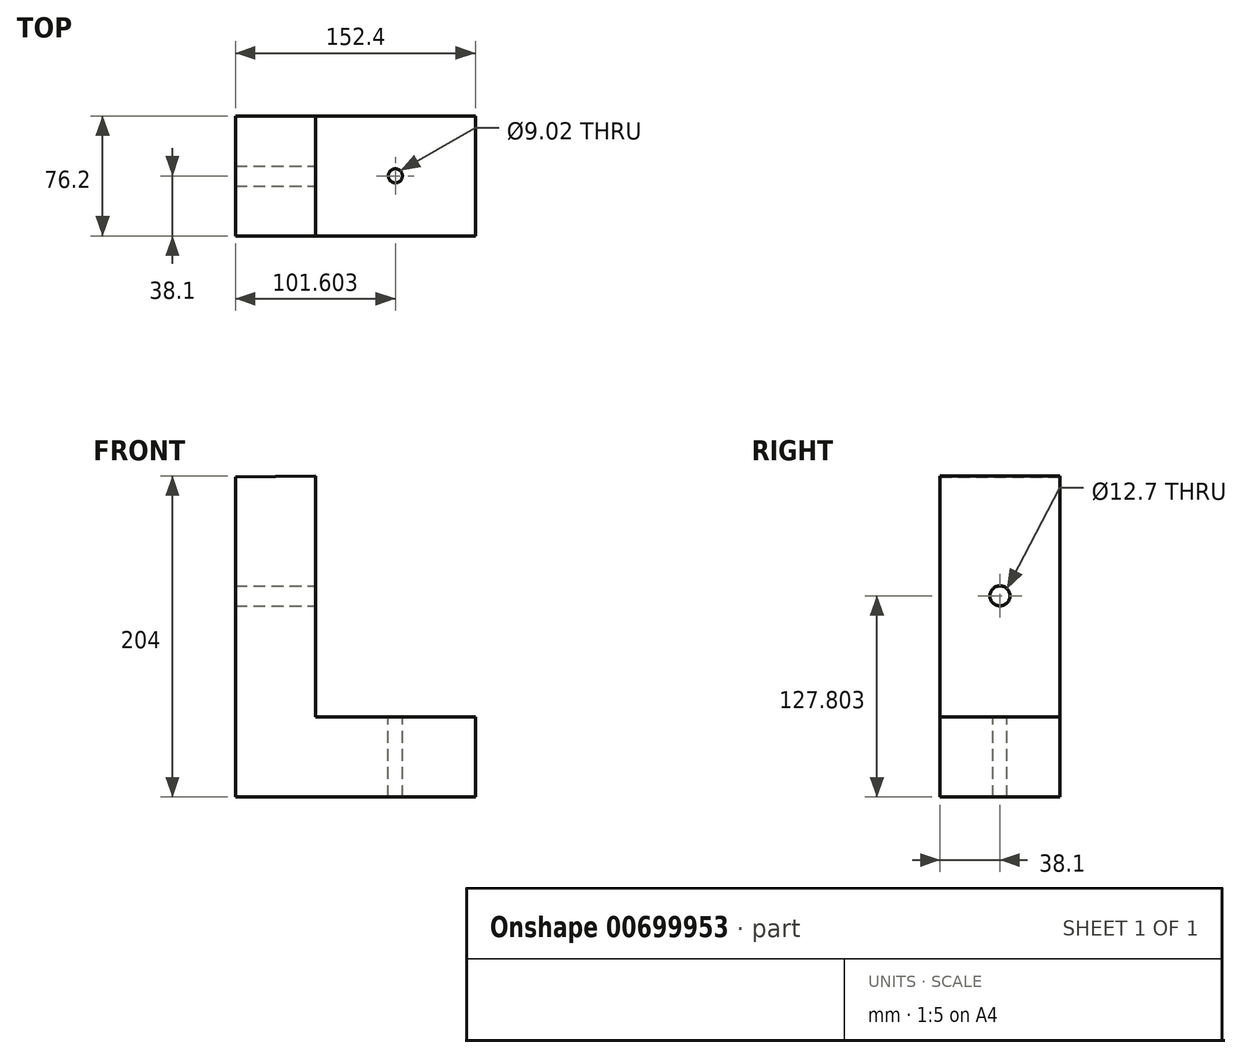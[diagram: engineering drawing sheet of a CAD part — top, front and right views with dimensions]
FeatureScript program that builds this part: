
annotation { "Feature Type Name" : "Feature", "Feature Type Description" : "" }
export const myFeature = defineFeature(function(context is Context, id is Id, definition is map)
    precondition{}
    {
        {
            var Q0;
            Q0=qCreatedBy(makeId("Front.planeOp"),FACE);
            var sketch = newSketch(context, id + "F0", { "sketchPlane" : qUnion([Q0])});
            skLineSegment(sketch, "E0", {"start": v(-81.87, 120.06) * mm, "end": v(-81.87, -83.14) * mm});
            skLineSegment(sketch, "E1", {"start": v(-81.87, -83.14) * mm, "end": v(70.53, -83.14) * mm});
            skLineSegment(sketch, "E2", {"start": v(70.53, -83.14) * mm, "end": v(70.53, -32.34) * mm});
            skLineSegment(sketch, "E3", {"start": v(70.53, -32.34) * mm, "end": v(-31.07, -32.34) * mm});
            skLineSegment(sketch, "E4", {"start": v(-31.07, -32.34) * mm, "end": v(-31.07, 120.86) * mm});
            skLineSegment(sketch, "E5", {"start": v(-31.07, 120.86) * mm, "end": v(-81.87, 120.06) * mm});
            skSolve(sketch);
        }
        {
            var Q0;
            Q0=makeQuery(id+"F0.imprint","IMPRINT",FACE,{"disambiguationData":[TD([[makeQuery(id+"F0.imprint","IMPRINT",EDGE,{"derivedFrom":sQuery(id+"F0.wireOp",EDGE,"E0")}),1.0]])]});
            extrude(context, id + "F1", {"entities" : qUnion([Q0]), "depth" : 76.2 * mm, "offsetDistance" : 25.4 * mm});
        }
        {
            var Q0;
            Q0=qCreatedBy(makeId("Right.planeOp"),FACE);
            var sketch = newSketch(context, id + "F2", { "sketchPlane" : qUnion([Q0])});
            skCircle(sketch, "E6", {"center": v(-38.1, 44.66) * mm, "radius": 6.35 * mm});
            skSolve(sketch);
        }
        {
            var Q0;
            Q0 = qSketchRegion(id + "F2", true);
            extrude(context, id + "F3", {"entities" : qUnion([Q0]), "operationType" : NewBodyOperationType.REMOVE, "oppositeDirection" : true, "depth" : 200.04 * mm, "offsetDistance" : 25.4 * mm});
        }
        {
            var Q0;
            Q0=qCreatedBy(makeId("Top.planeOp"),FACE);
            var sketch = newSketch(context, id + "F4", { "sketchPlane" : qUnion([Q0])});
            skCircle(sketch, "E7", {"center": v(19.73, -38.1) * mm, "radius": 4.5 * mm});
            skSolve(sketch);
        }
        {
            var Q0;
            Q0 = qSketchRegion(id + "F4", true);
            extrude(context, id + "F5", {"entities" : qUnion([Q0]), "operationType" : NewBodyOperationType.REMOVE, "oppositeDirection" : true, "depth" : 416.5 * mm, "offsetDistance" : 25.4 * mm});
        }
    });
